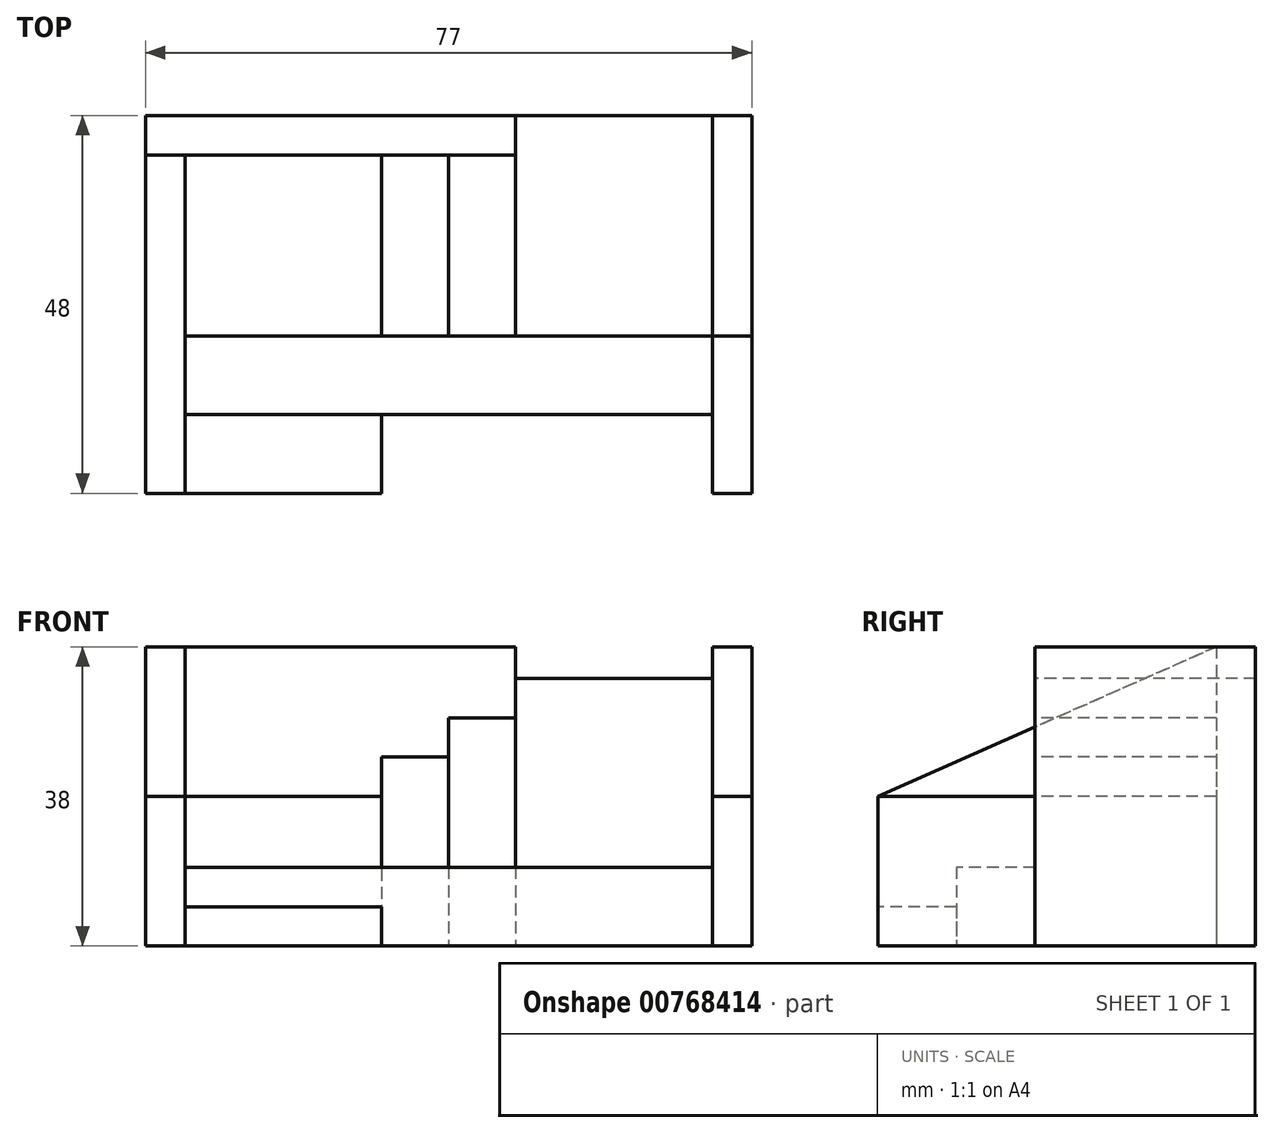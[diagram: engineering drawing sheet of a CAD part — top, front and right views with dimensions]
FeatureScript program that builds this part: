
annotation { "Feature Type Name" : "Feature", "Feature Type Description" : "" }
export const myFeature = defineFeature(function(context is Context, id is Id, definition is map)
    precondition{}
    {
        {
            var Q0;
            Q0=qCreatedBy(makeId("Top.planeOp"),FACE);
            var sketch = newSketch(context, id + "F0", { "sketchPlane" : qUnion([Q0])});
            skLineSegment(sketch, "E0.bottom", {"start": v(38.5, -24) * mm, "end": v(33.5, -24) * mm});
            skLineSegment(sketch, "E0.top", {"start": v(38.5, 24) * mm, "end": v(-38.5, 24) * mm});
            skLineSegment(sketch, "E0.left", {"start": v(38.5, -24) * mm, "end": v(38.5, 24) * mm});
            skLineSegment(sketch, "E0.right", {"start": v(-38.5, -24) * mm, "end": v(-38.5, 24) * mm});
            skPoint(sketch, "E0.middle", {"position": v(0, 0) * mm});
            skLineSegment(sketch, "E1", {"start": v(-33.5, 19) * mm, "end": v(-33.5, -24) * mm});
            skLineSegment(sketch, "E2", {"start": v(-38.5, 19) * mm, "end": v(8.5, 19) * mm});
            skLineSegment(sketch, "E3", {"start": v(-33.5, -14) * mm, "end": v(33.5, -14) * mm});
            skLineSegment(sketch, "E4", {"start": v(-33.5, -4) * mm, "end": v(38.5, -4) * mm});
            skLineSegment(sketch, "E5", {"start": v(-8.5, 19) * mm, "end": v(-8.5, -4) * mm});
            skLineSegment(sketch, "E6", {"start": v(8.5, 24) * mm, "end": v(8.5, -4) * mm});
            skLineSegment(sketch, "E7", {"start": v(33.5, 24) * mm, "end": v(33.5, -24) * mm});
            skLineSegment(sketch, "E8", {"start": v(0, 19) * mm, "end": v(0, -4) * mm});
            skPoint(sketch, "E9.orphan", {"position": v(-33.5, 24) * mm});
            skLineSegment(sketch, "E10.trimOffspring", {"start": v(-8.5, -14) * mm, "end": v(-8.5, -24) * mm});
            skLineSegment(sketch, "E11.trimOffspring", {"start": v(-8.5, -24) * mm, "end": v(-38.5, -24) * mm});
            skPoint(sketch, "E12.orphan", {"position": v(0, 24) * mm});
            skPoint(sketch, "E13.orphan", {"position": v(38.5, 19) * mm});
            skPoint(sketch, "E14.orphan", {"position": v(38.5, -14) * mm});
            skSolve(sketch);
        }
        {
            var Q0;
            {var subQ0=sQuery(id+"F0.wireOp",EDGE,"E11.trimOffspring");var subQ5=sQuery(id+"F0.wireOp",EDGE,"E0.right");var subQ6=makeQuery(id+"F0.imprint","INTERSECT",VERTEX,{"derivedFrom":[subQ5,subQ0]});Q0=makeQuery(id+"F0.imprint","IMPRINT",FACE,{"disambiguationData":[TD([[makeQuery(id+"F0.imprint","IMPRINT",EDGE,{"disambiguationData":[TD([[subQ6,-1.0]])],"derivedFrom":subQ5}),-1.0]])]});}
            extrude(context, id + "F1", {"entities" : qUnion([Q0]), "depth" : 38 * mm, "offsetDistance" : 25 * mm});
        }
        {
            var Q0;
            Q0=makeQuery(id+"F1.opExtrude","SWEPT_FACE",FACE,{"disambiguationData":[OSD([sQuery(id+"F0.wireOp",EDGE,"E1")])]});
            var sketch = newSketch(context, id + "F2", { "sketchPlane" : qUnion([Q0])});
            skLineSegment(sketch, "E15", {"start": v(19, 38) * mm, "end": v(-24, 19) * mm});
            skSolve(sketch);
        }
        {
            var Q0;
            {var subQ0=sQuery(id+"F2.wireOp",EDGE,"E15");Q0=makeQuery(id+"F2.imprint","IMPRINT",FACE,{"disambiguationData":[TD([[makeQuery(id+"F2.imprint","IMPRINT",EDGE,{"derivedFrom":subQ0}),-1.0]])]});}
            extrude(context, id + "F3", {"entities" : qUnion([Q0]), "operationType" : NewBodyOperationType.REMOVE, "oppositeDirection" : true, "depth" : 25 * mm, "offsetDistance" : 25 * mm});
        }
        {
            var Q0;
            {var subQ2=sQuery(id+"F0.wireOp",EDGE,"E0.right");var subQ7=sQuery(id+"F0.wireOp",EDGE,"E0.top");var subQ9=makeQuery(id+"F0.imprint","INTERSECT",VERTEX,{"derivedFrom":[subQ7,subQ2]});Q0=makeQuery(id+"F0.imprint","IMPRINT",FACE,{"disambiguationData":[TD([[makeQuery(id+"F0.imprint","IMPRINT",EDGE,{"disambiguationData":[TD([[subQ9,1.0]])],"derivedFrom":subQ7}),1.0]])]});}
            extrude(context, id + "F4", {"entities" : qUnion([Q0]), "operationType" : NewBodyOperationType.ADD, "depth" : 38 * mm, "offsetDistance" : 25 * mm});
        }
        {
            var Q0;
            {var subQ0=sQuery(id+"F0.wireOp",EDGE,"E0.left");var subQ1=sQuery(id+"F0.wireOp",EDGE,"E0.top");var subQ2=makeQuery(id+"F0.imprint","INTERSECT",VERTEX,{"derivedFrom":[subQ1,subQ0]});Q0=makeQuery(id+"F0.imprint","IMPRINT",FACE,{"disambiguationData":[TD([[makeQuery(id+"F0.imprint","IMPRINT",EDGE,{"disambiguationData":[TD([[subQ2,-1.0]])],"derivedFrom":subQ1}),1.0]])]});}
            extrude(context, id + "F5", {"entities" : qUnion([Q0]), "depth" : 38 * mm, "offsetDistance" : 25 * mm});
        }
        {
            var Q0;
            {var subQ0=sQuery(id+"F0.wireOp",EDGE,"E6");var subQ4=sQuery(id+"F0.wireOp",EDGE,"E0.top");var subQ5=makeQuery(id+"F0.imprint","INTERSECT",VERTEX,{"derivedFrom":[subQ4,subQ0]});Q0=makeQuery(id+"F0.imprint","IMPRINT",FACE,{"disambiguationData":[TD([[makeQuery(id+"F0.imprint","IMPRINT",EDGE,{"disambiguationData":[TD([[subQ5,1.0]])],"derivedFrom":subQ4}),1.0]])]});}
            extrude(context, id + "F6", {"entities" : qUnion([Q0]), "depth" : 34 * mm, "offsetDistance" : 25 * mm});
        }
        {
            var Q0;
            {var subQ3=sQuery(id+"F0.wireOp",EDGE,"E8");Q0=makeQuery(id+"F0.imprint","IMPRINT",FACE,{"disambiguationData":[TD([[makeQuery(id+"F0.imprint","IMPRINT",EDGE,{"derivedFrom":subQ3}),1.0]])]});}
            extrude(context, id + "F7", {"entities" : qUnion([Q0]), "depth" : 29 * mm, "offsetDistance" : 25 * mm});
        }
        {
            var Q0;
            {var subQ0=sQuery(id+"F0.wireOp",EDGE,"E5");Q0=makeQuery(id+"F0.imprint","IMPRINT",FACE,{"disambiguationData":[TD([[makeQuery(id+"F0.imprint","IMPRINT",EDGE,{"derivedFrom":subQ0}),1.0]])]});}
            extrude(context, id + "F8", {"entities" : qUnion([Q0]), "depth" : 24 * mm, "offsetDistance" : 25 * mm});
        }
        {
            var Q0;
            {var subQ5=sQuery(id+"F0.wireOp",EDGE,"E5");Q0=makeQuery(id+"F0.imprint","IMPRINT",FACE,{"disambiguationData":[TD([[makeQuery(id+"F0.imprint","IMPRINT",EDGE,{"derivedFrom":subQ5}),-1.0]])]});}
            extrude(context, id + "F9", {"entities" : qUnion([Q0]), "depth" : 19 * mm, "offsetDistance" : 25 * mm});
        }
        {
            var Q0;
            {var subQ1=sQuery(id+"F0.wireOp",EDGE,"E1");var subQ5=sQuery(id+"F0.wireOp",EDGE,"E3");var subQ8=makeQuery(id+"F0.imprint","INTERSECT",VERTEX,{"derivedFrom":[subQ1,subQ5]});Q0=makeQuery(id+"F0.imprint","IMPRINT",FACE,{"disambiguationData":[TD([[makeQuery(id+"F0.imprint","IMPRINT",EDGE,{"disambiguationData":[TD([[subQ8,1.0]])],"derivedFrom":subQ1}),1.0]])]});}
            extrude(context, id + "F10", {"entities" : qUnion([Q0]), "depth" : 10 * mm, "offsetDistance" : 25 * mm});
        }
        {
            var Q0;
            {var subQ5=sQuery(id+"F0.wireOp",EDGE,"E10.trimOffspring");Q0=makeQuery(id+"F0.imprint","IMPRINT",FACE,{"disambiguationData":[TD([[makeQuery(id+"F0.imprint","IMPRINT",EDGE,{"derivedFrom":subQ5}),-1.0]])]});}
            extrude(context, id + "F11", {"entities" : qUnion([Q0]), "depth" : 5 * mm, "offsetDistance" : 25 * mm});
        }
        {
            var Q0;
            {var subQ5=sQuery(id+"F0.wireOp",EDGE,"E0.bottom");Q0=makeQuery(id+"F0.imprint","IMPRINT",FACE,{"disambiguationData":[TD([[makeQuery(id+"F0.imprint","IMPRINT",EDGE,{"derivedFrom":subQ5}),-1.0]])]});}
            extrude(context, id + "F12", {"entities" : qUnion([Q0]), "depth" : 19 * mm, "offsetDistance" : 25 * mm});
        }
    });
